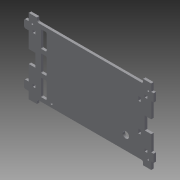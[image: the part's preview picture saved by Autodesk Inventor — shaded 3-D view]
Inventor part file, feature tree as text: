
AUTODESK INVENTOR PART (.ipt)
format: ipt  version: 2013 (Build 170138000, 138)  size: 280,064 bytes
history: native  units: mm
features: extrude x3, sketch x3
ambient origin geometry x8: Origin, YZ Plane, XZ Plane, XY Plane, X Axis, Y Axis, Z Axis, Center Point
bodies: Solid1 (feature_tree)
feature tree (6):
  extrude  "Extrusion1"  Depth=3.0mm
  extrude  "Extrusion5"  Depth=8.0mm
  extrude  "Extrusion8"  Depth=3.0mm
  sketch  "Sketch1"  dims[d5=10.0mm d20=3.0mm]
  sketch  "Sketch2"  dims[d42=47.0mm d43=3.0mm d44=8.0mm]
  sketch  "Sketch4"  dims[d45=81.0mm d47=3.0mm d49=10.0mm d50=10.0mm d52=3.0mm d53=6.0mm d54=6.0mm d56=5.0mm d57=5.0mm d58=85.0mm d59=3.0mm d60=0.0mm d61=93.0mm d63=19.5mm d65=9.5mm d74=2.0mm d75=8.0mm d76=8.0mm d77=16.0mm d78=36.5mm d79=3.0mm d80=3.0mm d81=3.0mm d82=3.0mm d83=5.0mm d84=5.0mm d85=27.5mm d86=27.5mm d89=8.0mm d90=5.0mm d91=5.0mm d92=27.5mm d93=27.5mm d94=3.0mm d95=3.0mm d96=3.0mm d97=3.0mm d113=5.0mm d114=10.0mm d115=10.0mm d116=5.0mm d117=10.0mm d118=10.0mm d119=2.0mm d120=6.0mm d124=41.5mm d127=6.0mm d128=80.0mm d129=3.0mm d130=132.0mm d133=3.0mm d135=33.0mm d136=93.0mm d140=16.0mm d142=8.0mm d144=10.0mm d145=5.0mm d146=5.0mm d147=27.5mm d148=27.5mm d149=27.5mm d150=27.5mm d151=5.0mm d152=3.0mm d153=5.0mm d154=3.0mm d155=30.0mm d159=10.0mm d160=0.0mm d161=16.0mm d162=16.0mm d164=161.0mm d165=31.5mm d167=17.0mm d168=8.0mm d169=3.0mm d170=3.0mm d171=144.0mm d172=4.0mm d173=31.5mm d176=3.0mm d177=74.0mm d179=4.5mm d181=4.5mm d184=4.5mm d185=21.0mm d186=7.0mm d187=15.0mm d188=5.0mm d189=21.0mm d190=7.0mm d191=5.0mm d192=15.0mm d193=21.0mm d194=5.0mm d195=15.0mm d196=7.0mm d197=1.0mm d200=3.0mm d201=4.5mm d202=24.0mm d203=10.0mm d204=0.0mm]
